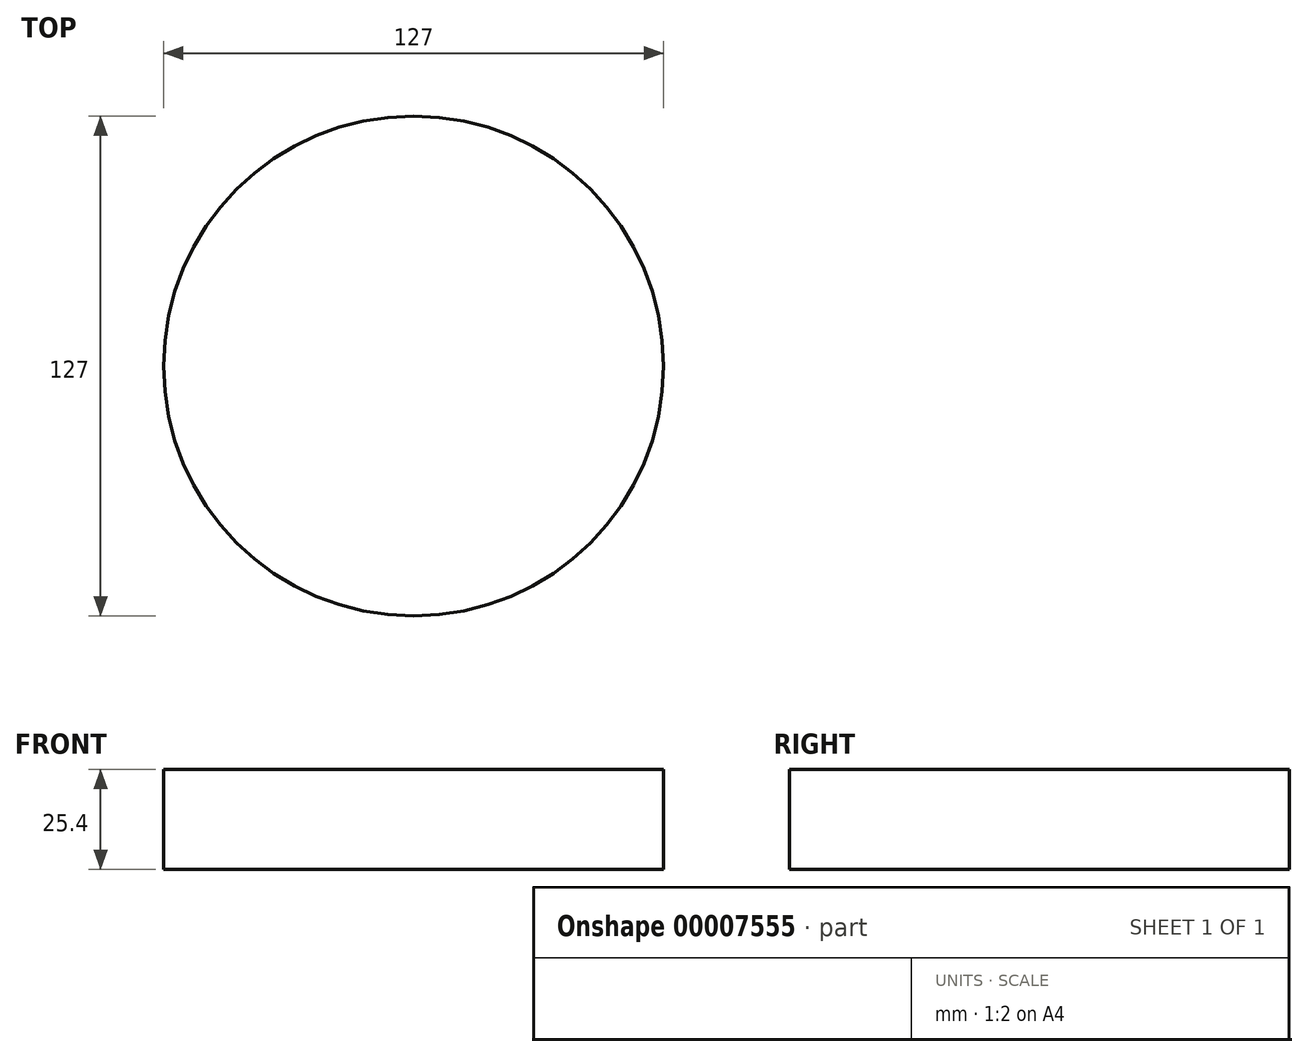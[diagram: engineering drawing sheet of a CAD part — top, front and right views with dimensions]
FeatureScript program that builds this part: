
annotation { "Feature Type Name" : "Feature", "Feature Type Description" : "" }
export const myFeature = defineFeature(function(context is Context, id is Id, definition is map)
    precondition{}
    {
        {
            var Q0;
            Q0=qCreatedBy(makeId("Top.planeOp"),FACE);
            var sketch = newSketch(context, id + "F0", { "sketchPlane" : qUnion([Q0])});
            skCircle(sketch, "E0", {"center": v(0, 0) * mm, "radius": 63.5 * mm});
            skSolve(sketch);
        }
        {
            var Q0;
            Q0 = qSketchRegion(id + "F0", true);
            extrude(context, id + "F1", {"entities" : qUnion([Q0]), "depth" : 25.4 * mm});
        }
    });
